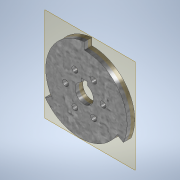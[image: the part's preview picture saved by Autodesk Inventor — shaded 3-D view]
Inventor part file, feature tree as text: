
AUTODESK INVENTOR PART (.ipt)
format: ipt  version: 2022 (Build 260153000, 153)  size: 226,304 bytes
history: native  units: in
note: dims shown in document units (in); Inventor stores cm internally (conversion verified against a paired STEP export)
features: sketch x2, extrude x2, pattern_circular x2, other x2, plane x1, thicken_offset x1, hole x1
ambient origin geometry x8: Origin, YZ Plane, XZ Plane, XY Plane, X Axis, Y Axis, Z Axis, Center Point
bodies: Solid1 (feature_tree)
feature tree (11):
  sketch  "Sketch1"  dims[d0=2.9528in d1=120.0deg]
  extrude  "Extrusion1"  TaperAngle=120.0deg  [1 undecoded]
  extrude  "Extrusion2"  Depth=0.25in TaperAngle=0.0deg
  pattern_circular  "Circular Pattern1"  Count=3 Angle=360.0deg
  plane  "Work Plane1"
  thicken_offset  "Thicken1"
  other  "A-Side Definition"
  hole  "Hole2"  [1 undecoded]
  pattern_circular  "Circular Pattern3"  [2 undecoded]
  sketch  "Sketch3"  dims[d2=0.2362in d3=0.25in d4=0.0in d5=1.1811in d6=360.0deg d8=0.5906in d20=0.1969in d21=0.1969in d22=0.25in d23=0.0in d24=0.005in d25=0.005in d26=0.6266in d27=0.3133in d28=0.1969in d29=0.75in d30=0.375in d31=0.25in d32=0.5635in d33=0.25in d34=0.0in d35=2.3622in d36=360.0deg]
  other  "Definition1"
note: 4 required parameter values undecoded (feature->parameter linkage not recoverable at this tier; creation-order binding heuristic only, values carry confidence <= 0.55)
